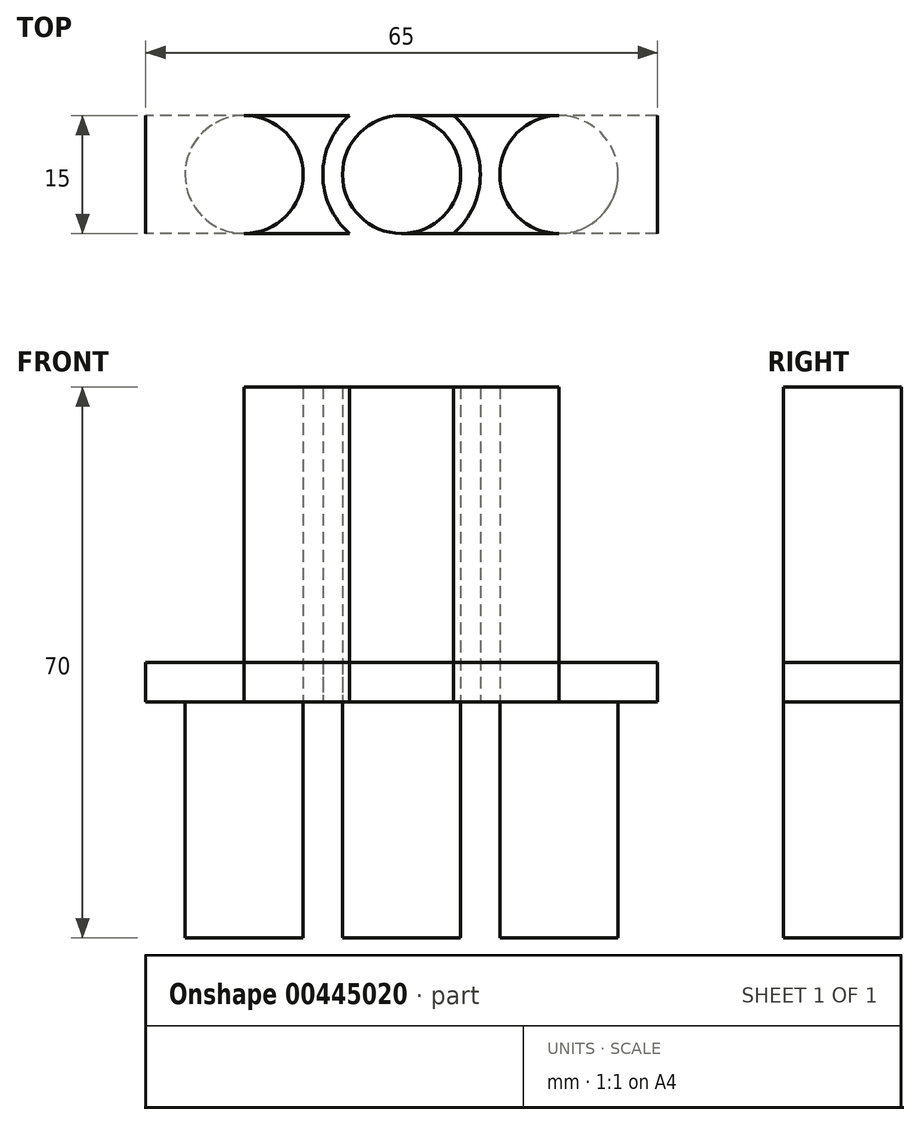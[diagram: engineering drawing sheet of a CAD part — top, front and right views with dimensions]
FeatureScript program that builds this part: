
annotation { "Feature Type Name" : "Feature", "Feature Type Description" : "" }
export const myFeature = defineFeature(function(context is Context, id is Id, definition is map)
    precondition{}
    {
        {
            var Q0;
            Q0=qCreatedBy(makeId("Top.planeOp"),FACE);
            var sketch = newSketch(context, id + "F0", { "sketchPlane" : qUnion([Q0])});
            skLineSegment(sketch, "E0.bottom", {"start": v(32.5, 7.5) * mm, "end": v(-32.5, 7.5) * mm});
            skLineSegment(sketch, "E0.top", {"start": v(32.5, -7.5) * mm, "end": v(-32.5, -7.5) * mm});
            skLineSegment(sketch, "E0.left", {"start": v(32.5, 7.5) * mm, "end": v(32.5, -7.5) * mm});
            skLineSegment(sketch, "E0.right", {"start": v(-32.5, 7.5) * mm, "end": v(-32.5, -7.5) * mm});
            skPoint(sketch, "E0.middle", {"position": v(0, 0) * mm});
            skCircle(sketch, "E1", {"center": v(0, 0) * mm, "radius": 7.5 * mm});
            skCircle(sketch, "E2", {"center": v(20, 0) * mm, "radius": 7.5 * mm});
            skCircle(sketch, "E3", {"center": v(-20, 0) * mm, "radius": 7.5 * mm});
            skCircle(sketch, "E4", {"center": v(0, 0) * mm, "radius": 10 * mm});
            skSolve(sketch);
        }
        {
            var Q0;
            {var subQ0=sQuery(id+"F0.wireOp",EDGE,"E0.right");Q0=makeQuery(id+"F0.imprint","IMPRINT",FACE,{"disambiguationData":[TD([[makeQuery(id+"F0.imprint","IMPRINT",EDGE,{"derivedFrom":subQ0}),1.0]])]});}
            var Q1;
            {var subQ0=sQuery(id+"F0.wireOp",EDGE,"E0.left");Q1=makeQuery(id+"F0.imprint","IMPRINT",FACE,{"disambiguationData":[TD([[makeQuery(id+"F0.imprint","IMPRINT",EDGE,{"derivedFrom":subQ0}),-1.0]])]});}
            var Q2;
            {var subQ0=sQuery(id+"F0.wireOp",EDGE,"E2");var subQ1=makeQuery(id+"F0.imprint","INTERSECT",VERTEX,{"derivedFrom":[sQuery(id+"F0.wireOp",EDGE,"E0.bottom"),subQ0]});Q2=makeQuery(id+"F0.imprint","IMPRINT",FACE,{"disambiguationData":[TD([[makeQuery(id+"F0.imprint","IMPRINT",EDGE,{"disambiguationData":[TD([[subQ1,-1.0]])],"derivedFrom":subQ0}),1.0]])]});}
            var Q3;
            {var subQ0=sQuery(id+"F0.wireOp",EDGE,"E4");var subQ1=sQuery(id+"F0.wireOp",EDGE,"E0.bottom");var subQ2=makeQuery(id+"F0.imprint","INTERSECT",VERTEX,{"disambiguationData":[OD(0.0)],"derivedFrom":[subQ1,subQ0]});Q3=makeQuery(id+"F0.imprint","IMPRINT",FACE,{"disambiguationData":[TD([[makeQuery(id+"F0.imprint","IMPRINT",EDGE,{"disambiguationData":[TD([[subQ2,-1.0]])],"derivedFrom":subQ1}),1.0]])]});}
            var Q4;
            {var subQ0=sQuery(id+"F0.wireOp",EDGE,"E2");var subQ1=sQuery(id+"F0.wireOp",EDGE,"E0.bottom");var subQ2=makeQuery(id+"F0.imprint","INTERSECT",VERTEX,{"derivedFrom":[subQ1,subQ0]});Q4=makeQuery(id+"F0.imprint","IMPRINT",FACE,{"disambiguationData":[TD([[makeQuery(id+"F0.imprint","IMPRINT",EDGE,{"disambiguationData":[TD([[subQ2,-1.0]])],"derivedFrom":subQ1}),1.0]])]});}
            var Q5;
            {var subQ0=sQuery(id+"F0.wireOp",EDGE,"E1");var subQ1=makeQuery(id+"F0.imprint","INTERSECT",VERTEX,{"derivedFrom":[sQuery(id+"F0.wireOp",EDGE,"E0.bottom"),subQ0]});Q5=makeQuery(id+"F0.imprint","IMPRINT",FACE,{"disambiguationData":[TD([[makeQuery(id+"F0.imprint","IMPRINT",EDGE,{"disambiguationData":[TD([[subQ1,-1.0]])],"derivedFrom":subQ0}),1.0]])]});}
            var Q6;
            {var subQ0=sQuery(id+"F0.wireOp",EDGE,"E4");var subQ1=sQuery(id+"F0.wireOp",EDGE,"E0.bottom");var subQ2=makeQuery(id+"F0.imprint","INTERSECT",VERTEX,{"disambiguationData":[OD(1.0)],"derivedFrom":[subQ1,subQ0]});Q6=makeQuery(id+"F0.imprint","IMPRINT",FACE,{"disambiguationData":[TD([[makeQuery(id+"F0.imprint","IMPRINT",EDGE,{"disambiguationData":[TD([[subQ2,1.0]])],"derivedFrom":subQ1}),1.0]])]});}
            var Q7;
            {var subQ0=sQuery(id+"F0.wireOp",EDGE,"E4");var subQ1=sQuery(id+"F0.wireOp",EDGE,"E0.bottom");var subQ2=makeQuery(id+"F0.imprint","INTERSECT",VERTEX,{"disambiguationData":[OD(1.0)],"derivedFrom":[subQ1,subQ0]});Q7=makeQuery(id+"F0.imprint","IMPRINT",FACE,{"disambiguationData":[TD([[makeQuery(id+"F0.imprint","IMPRINT",EDGE,{"disambiguationData":[TD([[subQ2,-1.0]])],"derivedFrom":subQ1}),1.0]])]});}
            var Q8;
            {var subQ0=sQuery(id+"F0.wireOp",EDGE,"E3");var subQ1=makeQuery(id+"F0.imprint","INTERSECT",VERTEX,{"derivedFrom":[sQuery(id+"F0.wireOp",EDGE,"E0.bottom"),subQ0]});Q8=makeQuery(id+"F0.imprint","IMPRINT",FACE,{"disambiguationData":[TD([[makeQuery(id+"F0.imprint","IMPRINT",EDGE,{"disambiguationData":[TD([[subQ1,-1.0]])],"derivedFrom":subQ0}),1.0]])]});}
            extrude(context, id + "F1", {"entities" : qUnion([Q0, Q1, Q2, Q3, Q4, Q5, Q6, Q7, Q8]), "depth" : 5 * mm});
        }
        {
            var Q0;
            {var subQ0=sQuery(id+"F0.wireOp",EDGE,"E3");var subQ1=makeQuery(id+"F0.imprint","INTERSECT",VERTEX,{"derivedFrom":[sQuery(id+"F0.wireOp",EDGE,"E0.bottom"),subQ0]});Q0=makeQuery(id+"F0.imprint","IMPRINT",FACE,{"disambiguationData":[TD([[makeQuery(id+"F0.imprint","IMPRINT",EDGE,{"disambiguationData":[TD([[subQ1,-1.0]])],"derivedFrom":subQ0}),1.0]])]});}
            var Q1;
            {var subQ0=sQuery(id+"F0.wireOp",EDGE,"E1");var subQ1=makeQuery(id+"F0.imprint","INTERSECT",VERTEX,{"derivedFrom":[sQuery(id+"F0.wireOp",EDGE,"E0.bottom"),subQ0]});Q1=makeQuery(id+"F0.imprint","IMPRINT",FACE,{"disambiguationData":[TD([[makeQuery(id+"F0.imprint","IMPRINT",EDGE,{"disambiguationData":[TD([[subQ1,-1.0]])],"derivedFrom":subQ0}),1.0]])]});}
            var Q2;
            {var subQ0=sQuery(id+"F0.wireOp",EDGE,"E2");var subQ1=makeQuery(id+"F0.imprint","INTERSECT",VERTEX,{"derivedFrom":[sQuery(id+"F0.wireOp",EDGE,"E0.bottom"),subQ0]});Q2=makeQuery(id+"F0.imprint","IMPRINT",FACE,{"disambiguationData":[TD([[makeQuery(id+"F0.imprint","IMPRINT",EDGE,{"disambiguationData":[TD([[subQ1,-1.0]])],"derivedFrom":subQ0}),1.0]])]});}
            extrude(context, id + "F2", {"entities" : qUnion([Q0, Q1, Q2]), "operationType" : NewBodyOperationType.ADD, "oppositeDirection" : true, "depth" : 30 * mm});
        }
        {
            var Q0;
            {var subQ0=sQuery(id+"F0.wireOp",EDGE,"E1");var subQ1=makeQuery(id+"F0.imprint","INTERSECT",VERTEX,{"derivedFrom":[sQuery(id+"F0.wireOp",EDGE,"E0.bottom"),subQ0]});Q0=makeQuery(id+"F0.imprint","IMPRINT",FACE,{"disambiguationData":[TD([[makeQuery(id+"F0.imprint","IMPRINT",EDGE,{"disambiguationData":[TD([[subQ1,-1.0]])],"derivedFrom":subQ0}),1.0]])]});}
            var Q1;
            {var subQ0=sQuery(id+"F0.wireOp",EDGE,"E4");var subQ1=sQuery(id+"F0.wireOp",EDGE,"E0.bottom");var subQ2=makeQuery(id+"F0.imprint","INTERSECT",VERTEX,{"disambiguationData":[OD(0.0)],"derivedFrom":[subQ1,subQ0]});Q1=makeQuery(id+"F0.imprint","IMPRINT",FACE,{"disambiguationData":[TD([[makeQuery(id+"F0.imprint","IMPRINT",EDGE,{"disambiguationData":[TD([[subQ2,-1.0]])],"derivedFrom":subQ1}),1.0]])]});}
            var Q2;
            {var subQ0=sQuery(id+"F0.wireOp",EDGE,"E4");var subQ1=sQuery(id+"F0.wireOp",EDGE,"E0.bottom");var subQ2=makeQuery(id+"F0.imprint","INTERSECT",VERTEX,{"disambiguationData":[OD(1.0)],"derivedFrom":[subQ1,subQ0]});Q2=makeQuery(id+"F0.imprint","IMPRINT",FACE,{"disambiguationData":[TD([[makeQuery(id+"F0.imprint","IMPRINT",EDGE,{"disambiguationData":[TD([[subQ2,1.0]])],"derivedFrom":subQ1}),1.0]])]});}
            var Q3;
            {var subQ0=sQuery(id+"F0.wireOp",EDGE,"E4");var subQ1=sQuery(id+"F0.wireOp",EDGE,"E0.bottom");var subQ2=makeQuery(id+"F0.imprint","INTERSECT",VERTEX,{"disambiguationData":[OD(0.0)],"derivedFrom":[subQ1,subQ0]});Q3=makeQuery(id+"F0.imprint","IMPRINT",FACE,{"disambiguationData":[TD([[makeQuery(id+"F0.imprint","IMPRINT",EDGE,{"disambiguationData":[TD([[subQ2,-1.0]])],"derivedFrom":subQ1}),-1.0]])]});}
            var Q4;
            {var subQ0=sQuery(id+"F0.wireOp",EDGE,"E4");var subQ1=sQuery(id+"F0.wireOp",EDGE,"E0.top");var subQ2=makeQuery(id+"F0.imprint","INTERSECT",VERTEX,{"disambiguationData":[OD(0.0)],"derivedFrom":[subQ1,subQ0]});Q4=makeQuery(id+"F0.imprint","IMPRINT",FACE,{"disambiguationData":[TD([[makeQuery(id+"F0.imprint","IMPRINT",EDGE,{"disambiguationData":[TD([[subQ2,-1.0]])],"derivedFrom":subQ1}),1.0]])]});}
            extrude(context, id + "F3", {"entities" : qUnion([Q0, Q1, Q2, Q3, Q4]), "depth" : 40 * mm});
        }
    });
